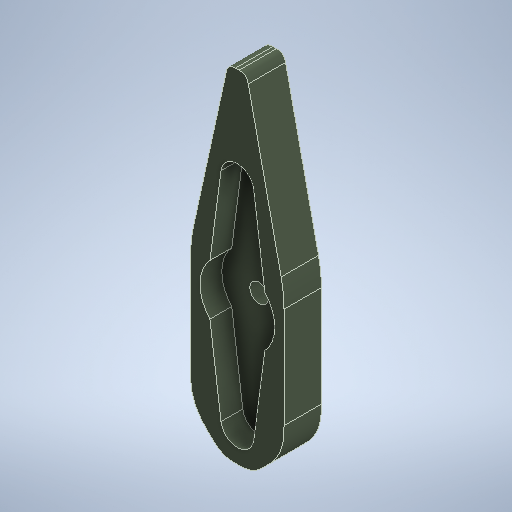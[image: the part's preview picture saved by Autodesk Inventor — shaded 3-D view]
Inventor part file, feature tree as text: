
AUTODESK INVENTOR PART (.ipt)
format: ipt  version: 2025.1 (Build 291241000, 241)  size: 331,264 bytes
history: native  units: in
note: dims shown in document units (in); Inventor stores cm internally (conversion verified against a paired STEP export)
features: fillet x4, extrude x3, chamfer x3, sketch x1
ambient origin geometry x8: Origin, YZ Plane, XZ Plane, XY Plane, X Axis, Y Axis, Z Axis, Center Point
bodies: Solid1 (feature_tree)
feature tree (11):
  sketch  "Sketch1"  dims[d0=0.0669in d1=0.0669in d2=0.6732in d3=0.2087in d4=0.2087in d5=0.4724in d6=0.3465in d7=0.3465in d8=0.1181in d9=0.315in d10=0.1969in d11=2.1654in d12=0.5906in d13=0.2362in d14=0.0in d15=0.0984in d16=0.0in d17=0.2362in d18=0.0in d20=0.2362in d21=1.0827in d22=45.0deg d23=1.0827in d24=0.2362in d25=45.0deg d26=0.1969in d27=0.2362in d28=45.0deg d30=0.0591in d31=0.7874in d32=0.3937in d33=0.2362in]
  extrude  "Extrusion1"  Depth=0.1969in
  extrude  "Extrusion2"  Depth=2.1654in
  extrude  "Extrusion3"  Depth=0.5906in
  chamfer  "Chamfer1"  Distance=0.2362in
  chamfer  "Chamfer2"  Distance=0.0984in
  chamfer  "Chamfer3"  Distance=0.2362in
  fillet  "Fillet3"  Radius=0.2362in
  fillet  "Fillet4"  Radius=1.0827in
  fillet  "Fillet5"  Radius=0.1969in
  fillet  "Fillet6"  Radius=0.0591in
